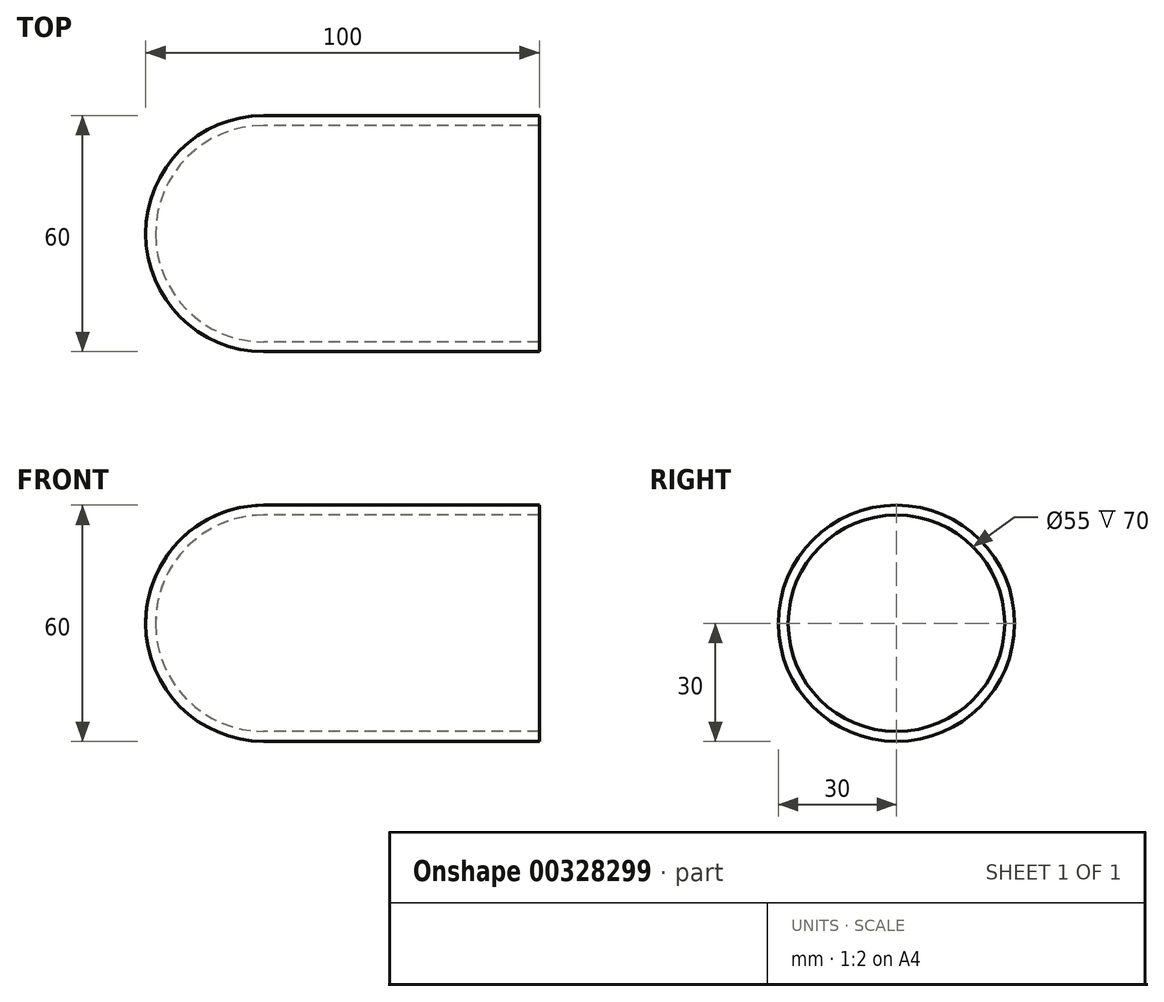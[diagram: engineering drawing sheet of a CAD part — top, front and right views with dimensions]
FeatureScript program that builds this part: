
annotation { "Feature Type Name" : "Feature", "Feature Type Description" : "" }
export const myFeature = defineFeature(function(context is Context, id is Id, definition is map)
    precondition{}
    {
        {
            var Q0;
            Q0=qCreatedBy(makeId("Front.planeOp"),FACE);
            var sketch = newSketch(context, id + "F0", { "sketchPlane" : qUnion([Q0])});
            skLineSegment(sketch, "E0", {"start": v(0, 30) * mm, "end": v(70, 30) * mm});
            skArc(sketch, "E1", {"start": v(0, 30) * mm, "mid": v(-21.21, 21.21) * mm, "end": v(-30, 0) * mm});
            skLineSegment(sketch, "E2", {"start": v(-30, 0) * mm, "end": v(70, 0) * mm, "construction": true});
            skLineSegment(sketch, "E3", {"start": v(-30, 0) * mm, "end": v(70, 0) * mm});
            skLineSegment(sketch, "E4", {"start": v(70, 30) * mm, "end": v(70, 0) * mm});
            skSolve(sketch);
        }
        {
            var Q0;
            Q0 = qSketchRegion(id + "F0", true);
            var Q1;
            Q1=sQuery(id+"F0.wireOp",EDGE,"E3");
            revolve(context, id + "F1", {"entities" : qUnion([Q0]), "axis" : qUnion([Q1]), "revolveType" : RevolveType.FULL});
        }
        {
            var Q0;
            Q0=makeQuery(id+"F1.opRevolve","SWEPT_FACE",FACE,{"disambiguationData":[OSD([sQuery(id+"F0.wireOp",EDGE,"E4")])]});
            shell(context, id + "F2", {"entities" : qUnion([Q0]), "thickness" : 2.5 * mm});
        }
    });
